FCSTD DOCUMENT  (FreeCAD 0.22R38314 (Git))
Label: hole 1
License: All rights reserved
LicenseURL: http://en.wikipedia.org/wiki/All_rights_reserved
objects: Part::Feature×2, Part::Box×1, Sketcher::SketchObject×1, PartDesign::Body×1
note: 5 computed .brp shape members not serialized (recipe doc carries the construction recipe); baked Part::Feature solids carry a one-line shape summary decoded from their .brp

FEATURE [Part::Feature] Part__Feature132  label="body_e"
  shape: bbox 273.6 x 255.4 x 85.46 mm, 1133 faces (baked)
FEATURE [Part::Feature] Part__Feature133  label="body_s"
  shape: bbox 273.6 x 255.4 x 67.48 mm, 841 faces (baked)
FEATURE [Part::Box] Box  label="Cube"
  AttacherType = Attacher::AttachEngine3D
  Height = 84
  Length = 7
  Placement = pos=(-211.692,-69.4995,-59) rot=(0,0,-1;5.58505rad)
  Width = 43
FEATURE [Sketcher::SketchObject] Sketch
  FullyConstrained = false
  MapMode = 5
  Placement = pos=(-149.453,-129.917,0) rot=(0.840552,-0.383062,-0.383062;1.74363rad)
  sketch-geometry (9):
    g0: Circle CenterX=-123.246 CenterY=-36.8499 CenterZ=0 NormalX=0 NormalY=0 NormalZ=1 AngleXU=0 Radius=0.854039
    g1: Circle CenterX=-93.2538 CenterY=-36.8455 CenterZ=0 NormalX=0 NormalY=0 NormalZ=1 AngleXU=0 Radius=0.847497
    g2: Circle CenterX=-93.2484 CenterY=-10.2467 CenterZ=0 NormalX=0 NormalY=0 NormalZ=1 AngleXU=0 Radius=0.84879
    g3: Circle CenterX=-123.242 CenterY=-10.2435 CenterZ=0 NormalX=0 NormalY=0 NormalZ=1 AngleXU=0 Radius=0.850126
    g4: ArcOfCircle CenterX=-123.211 CenterY=-10.2993 CenterZ=0 NormalX=0 NormalY=0 NormalZ=1 AngleXU=0 Radius=3.03953 StartAngle=1.58585 EndAngle=3.12898
    g5: ArcOfCircle CenterX=-93.2928 CenterY=-10.2943 CenterZ=0 NormalX=0 NormalY=0 NormalZ=1 AngleXU=0 Radius=3.04094 StartAngle=0.0107 EndAngle=1.55767
    g6: ArcOfCircle CenterX=-93.293 CenterY=-36.7977 CenterZ=0 NormalX=0 NormalY=0 NormalZ=1 AngleXU=0 Radius=3.03496 StartAngle=4.72605 EndAngle=6.27396
    g7: ArcOfCircle CenterX=-123.225 CenterY=-36.8474 CenterZ=0 NormalX=0 NormalY=0 NormalZ=1 AngleXU=0 Radius=3.02355 StartAngle=3.14729 EndAngle=4.70127
    g8: ArcOfCircle CenterX=-123.179 CenterY=-36.85 CenterZ=0 NormalX=0 NormalY=0 NormalZ=1 AngleXU=0 Radius=5.0197 StartAngle=3.14451 EndAngle=4.70296
FEATURE [PartDesign::Body] Body
  AllowCompound = false
  Group = -> [Sketch]
  Origin = -> Origin
